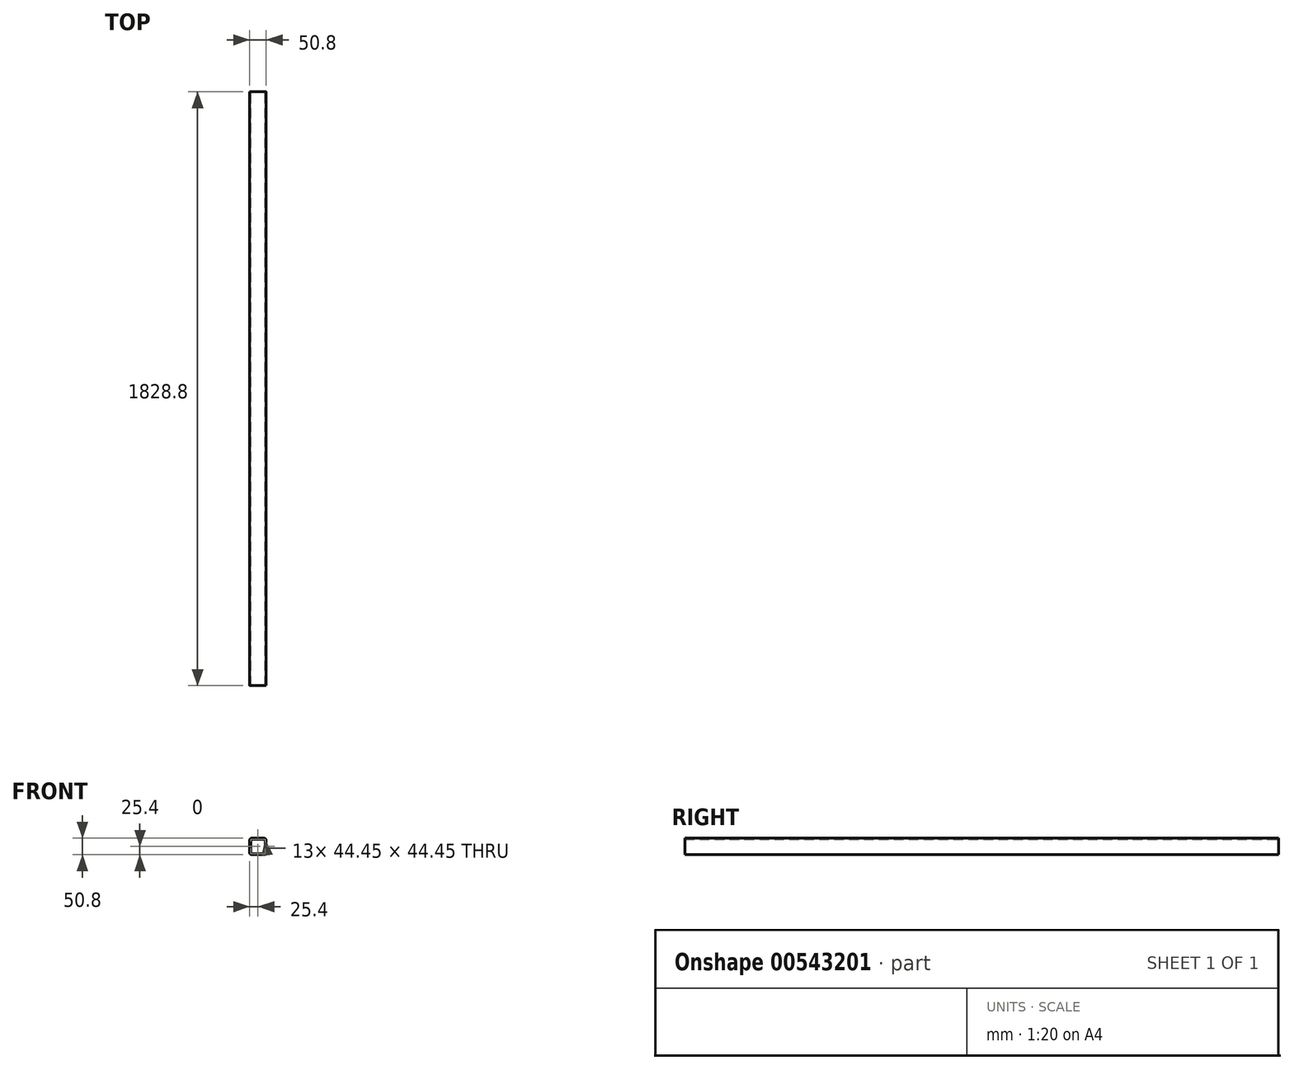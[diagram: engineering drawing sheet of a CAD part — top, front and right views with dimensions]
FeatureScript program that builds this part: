
annotation { "Feature Type Name" : "Feature", "Feature Type Description" : "" }
export const myFeature = defineFeature(function(context is Context, id is Id, definition is map)
    precondition{}
    {
        {
            var Q0;
            Q0=qCreatedBy(makeId("Front.planeOp"),FACE);
            var sketch = newSketch(context, id + "F0", { "sketchPlane" : qUnion([Q0])});
            skPoint(sketch, "E0.middle", {"position": v(0, 0) * mm});
            skLineSegment(sketch, "E1.bottom", {"start": v(19.05, 25.4) * mm, "end": v(-19.05, 25.4) * mm});
            skLineSegment(sketch, "E1.top", {"start": v(19.05, -25.4) * mm, "end": v(-19.05, -25.4) * mm});
            skLineSegment(sketch, "E1.left", {"start": v(25.4, 19.05) * mm, "end": v(25.4, -19.05) * mm});
            skLineSegment(sketch, "E1.right", {"start": v(-25.4, 19.05) * mm, "end": v(-25.4, -19.05) * mm});
            skLineSegment(sketch, "E2.bottom", {"start": v(22.23, 22.23) * mm, "end": v(-22.23, 22.23) * mm});
            skLineSegment(sketch, "E2.top", {"start": v(22.23, -22.23) * mm, "end": v(-22.23, -22.23) * mm});
            skLineSegment(sketch, "E2.left", {"start": v(22.23, 22.23) * mm, "end": v(22.23, -22.23) * mm});
            skLineSegment(sketch, "E2.right", {"start": v(-22.23, 22.23) * mm, "end": v(-22.23, -22.23) * mm});
            skPoint(sketch, "E3.visualSharp", {"position": v(25.4, 25.4) * mm});
            skArc(sketch, "E3.filletArc", {"start": v(25.4, 19.05) * mm, "mid": v(23.54, 23.54) * mm, "end": v(19.05, 25.4) * mm});
            skPoint(sketch, "E4.visualSharp", {"position": v(-25.4, 25.4) * mm});
            skArc(sketch, "E4.filletArc", {"start": v(-19.05, 25.4) * mm, "mid": v(-23.54, 23.54) * mm, "end": v(-25.4, 19.05) * mm});
            skPoint(sketch, "E5.visualSharp", {"position": v(-25.4, -25.4) * mm});
            skArc(sketch, "E5.filletArc", {"start": v(-25.4, -19.05) * mm, "mid": v(-23.54, -23.54) * mm, "end": v(-19.05, -25.4) * mm});
            skPoint(sketch, "E6.visualSharp", {"position": v(25.4, -25.4) * mm});
            skArc(sketch, "E6.filletArc", {"start": v(19.05, -25.4) * mm, "mid": v(23.54, -23.54) * mm, "end": v(25.4, -19.05) * mm});
            skSolve(sketch);
        }
        {
            var Q0;
            Q0 = qSketchRegion(id + "F0", true);
            extrude(context, id + "F1", {"entities" : qUnion([Q0]), "depth" : 1828.8 * mm, "offsetDistance" : 25.4 * mm});
        }
    });
